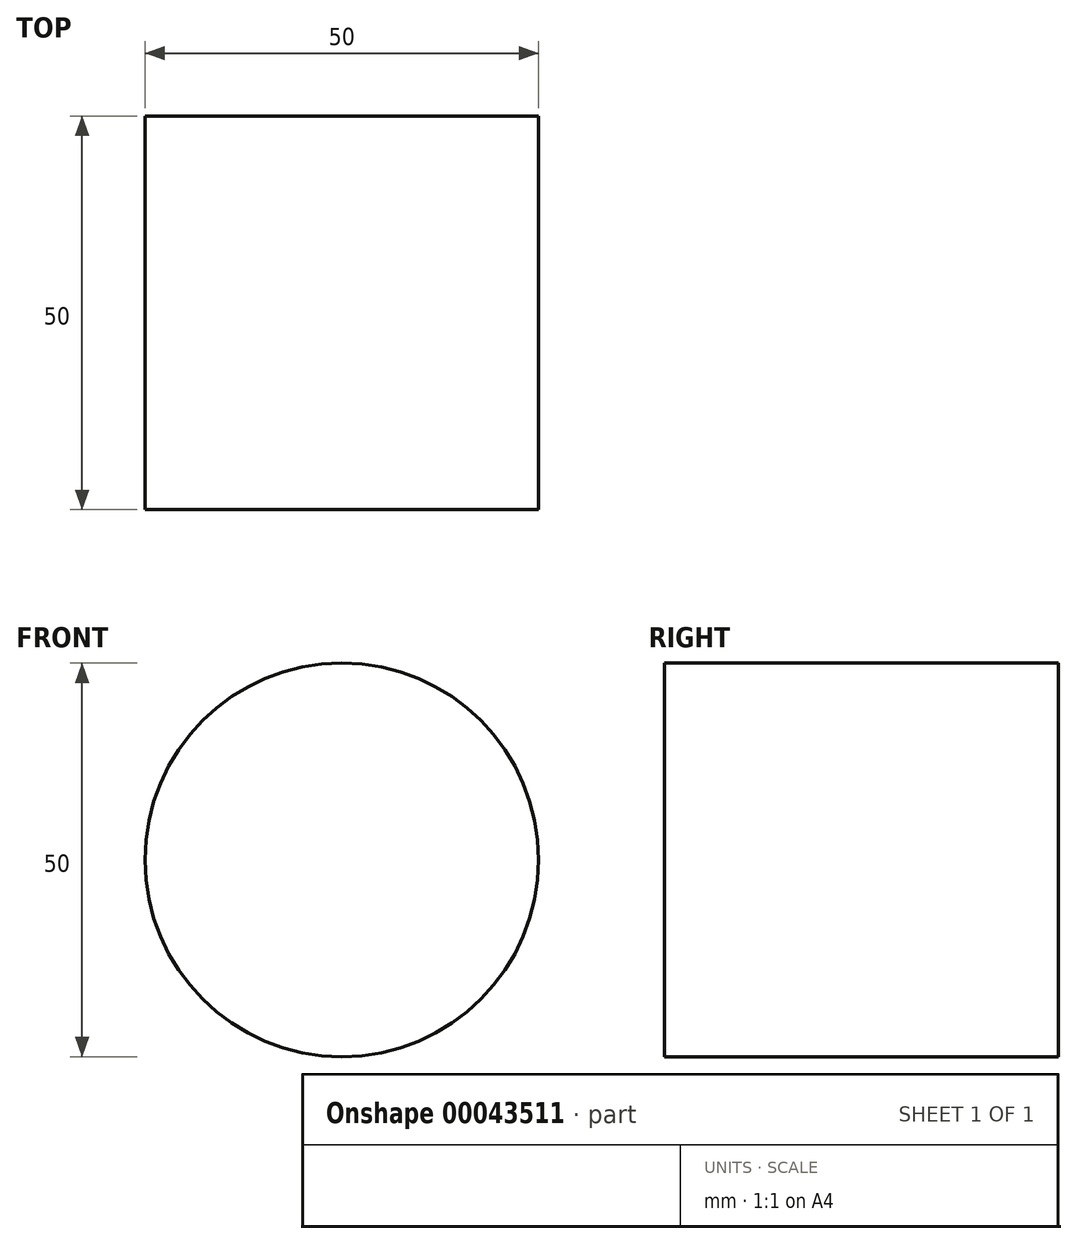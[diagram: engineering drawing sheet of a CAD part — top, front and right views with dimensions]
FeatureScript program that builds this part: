
annotation { "Feature Type Name" : "Feature", "Feature Type Description" : "" }
export const myFeature = defineFeature(function(context is Context, id is Id, definition is map)
    precondition{}
    {
        {
            var Q0;
            Q0=qCreatedBy(makeId("Front.planeOp"),FACE);
            var sketch = newSketch(context, id + "F0", { "sketchPlane" : qUnion([Q0])});
            skCircle(sketch, "E0", {"center": v(-35.65, 24.5) * mm, "radius": 25 * mm});
            skSolve(sketch);
        }
        {
            var Q0;
            Q0=makeQuery(id+"F0.imprint","IMPRINT",FACE,{"disambiguationData":[TD([[makeQuery(id+"F0.imprint","IMPRINT",EDGE,{"derivedFrom":sQuery(id+"F0.wireOp",EDGE,"E0")}),1.0]])]});
            extrude(context, id + "F1", {"entities" : qUnion([Q0]), "depth" : 50 * mm});
        }
    });
